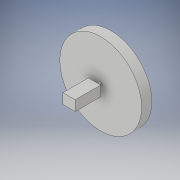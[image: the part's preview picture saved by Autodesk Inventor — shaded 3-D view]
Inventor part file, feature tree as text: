
AUTODESK INVENTOR PART (.ipt)
format: ipt  version: 2018 (Build 220112000, 112)  size: 114,176 bytes
history: native  units: mm
features: extrude x3, sketch x3, projected_geometry x1
ambient origin geometry x8: Origin, YZ Plane, XZ Plane, XY Plane, X Axis, Y Axis, Z Axis, Center Point
bodies: Solid1 (feature_tree)
feature tree (7):
  extrude  "Extrusion1"  Depth=25.0mm
  extrude  "Extrusion2"  Depth=10.0mm
  extrude  "Extrusion3"  Depth=10.0mm
  sketch  "Sketch1"  dims[d0=12.0mm d1=25.0mm]
  sketch  "Sketch2"  dims[d2=10.0mm d3=0.0mm d4=3.0mm]
  projected_geometry  "Projected Loop1"
  sketch  "Sketch3"  dims[d5=6.0mm d6=0.0mm d7=80.0mm d8=10.0mm d9=0.0mm]
